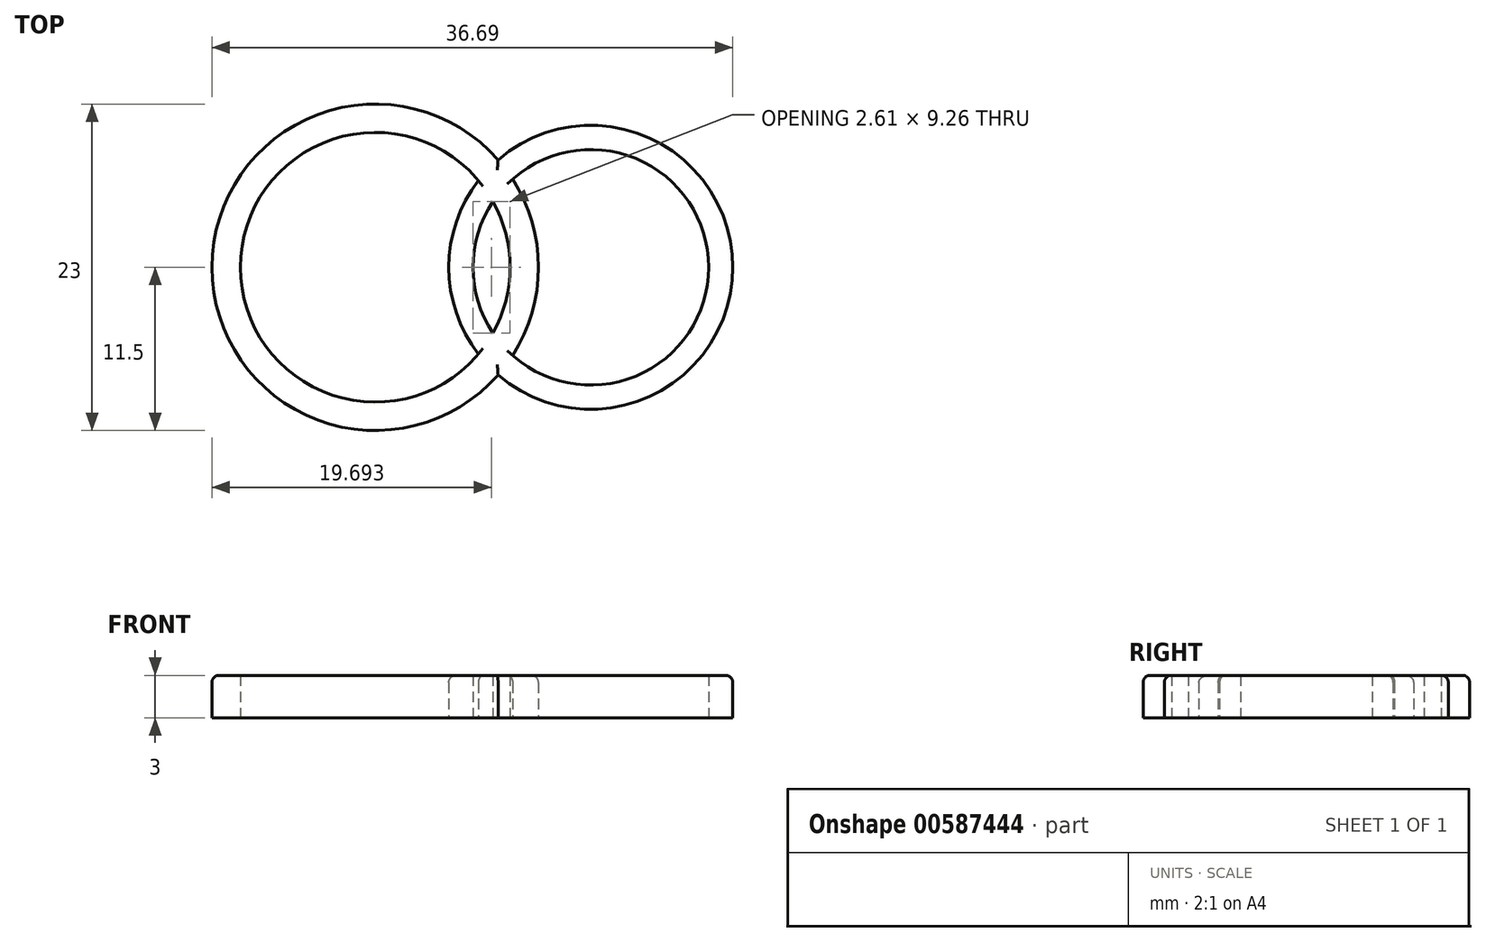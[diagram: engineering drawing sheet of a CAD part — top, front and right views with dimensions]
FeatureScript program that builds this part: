
annotation { "Feature Type Name" : "Feature", "Feature Type Description" : "" }
export const myFeature = defineFeature(function(context is Context, id is Id, definition is map)
    precondition{}
    {
        {
            var Q0;
            Q0=qCreatedBy(makeId("Top.planeOp"),FACE);
            var sketch = newSketch(context, id + "F0", { "sketchPlane" : qUnion([Q0])});
            skCircle(sketch, "E0", {"center": v(0, 0) * mm, "radius": 11.5 * mm});
            skCircle(sketch, "E1", {"center": v(0, 0) * mm, "radius": 9.5 * mm});
            skCircle(sketch, "E2", {"center": v(15.19, 0) * mm, "radius": 10 * mm});
            skCircle(sketch, "E3", {"center": v(15.19, 0) * mm, "radius": 8.3 * mm});
            skSolve(sketch);
        }
        {
            var Q0;
            {var subQ0=sQuery(id+"F0.wireOp",EDGE,"E2");var subQ1=sQuery(id+"F0.wireOp",EDGE,"E0");var subQ2=makeQuery(id+"F0.imprint","INTERSECT",VERTEX,{"disambiguationData":[OD(0.0)],"derivedFrom":[subQ1,subQ0]});Q0=makeQuery(id+"F0.imprint","IMPRINT",FACE,{"disambiguationData":[TD([[makeQuery(id+"F0.imprint","IMPRINT",EDGE,{"disambiguationData":[TD([[subQ2,-1.0]])],"derivedFrom":subQ1}),1.0]])]});}
            var Q1;
            {var subQ0=sQuery(id+"F0.wireOp",EDGE,"E2");var subQ1=sQuery(id+"F0.wireOp",EDGE,"E0");var subQ2=makeQuery(id+"F0.imprint","INTERSECT",VERTEX,{"disambiguationData":[OD(0.0)],"derivedFrom":[subQ1,subQ0]});Q1=makeQuery(id+"F0.imprint","IMPRINT",FACE,{"disambiguationData":[TD([[makeQuery(id+"F0.imprint","IMPRINT",EDGE,{"disambiguationData":[TD([[subQ2,1.0]])],"derivedFrom":subQ1}),1.0]])]});}
            var Q2;
            {var subQ0=sQuery(id+"F0.wireOp",EDGE,"E3");var subQ1=sQuery(id+"F0.wireOp",EDGE,"E0");var subQ2=makeQuery(id+"F0.imprint","INTERSECT",VERTEX,{"disambiguationData":[OD(0.0)],"derivedFrom":[subQ1,subQ0]});Q2=makeQuery(id+"F0.imprint","IMPRINT",FACE,{"disambiguationData":[TD([[makeQuery(id+"F0.imprint","IMPRINT",EDGE,{"disambiguationData":[TD([[subQ2,1.0]])],"derivedFrom":subQ1}),1.0]])]});}
            var Q3;
            {var subQ0=sQuery(id+"F0.wireOp",EDGE,"E2");var subQ1=sQuery(id+"F0.wireOp",EDGE,"E0");var subQ2=makeQuery(id+"F0.imprint","INTERSECT",VERTEX,{"disambiguationData":[OD(1.0)],"derivedFrom":[subQ1,subQ0]});Q3=makeQuery(id+"F0.imprint","IMPRINT",FACE,{"disambiguationData":[TD([[makeQuery(id+"F0.imprint","IMPRINT",EDGE,{"disambiguationData":[TD([[subQ2,-1.0]])],"derivedFrom":subQ1}),1.0]])]});}
            var Q4;
            {var subQ0=sQuery(id+"F0.wireOp",EDGE,"E2");var subQ1=sQuery(id+"F0.wireOp",EDGE,"E1");var subQ2=makeQuery(id+"F0.imprint","INTERSECT",VERTEX,{"disambiguationData":[OD(0.0)],"derivedFrom":[subQ1,subQ0]});Q4=makeQuery(id+"F0.imprint","IMPRINT",FACE,{"disambiguationData":[TD([[makeQuery(id+"F0.imprint","IMPRINT",EDGE,{"disambiguationData":[TD([[subQ2,1.0]])],"derivedFrom":subQ1}),1.0]])]});}
            var Q5;
            {var subQ0=sQuery(id+"F0.wireOp",EDGE,"E2");var subQ1=sQuery(id+"F0.wireOp",EDGE,"E0");var subQ2=makeQuery(id+"F0.imprint","INTERSECT",VERTEX,{"disambiguationData":[OD(0.0)],"derivedFrom":[subQ1,subQ0]});Q5=makeQuery(id+"F0.imprint","IMPRINT",FACE,{"disambiguationData":[TD([[makeQuery(id+"F0.imprint","IMPRINT",EDGE,{"disambiguationData":[TD([[subQ2,1.0]])],"derivedFrom":subQ1}),-1.0]])]});}
            extrude(context, id + "F1", {"entities" : qUnion([Q0, Q1, Q2, Q3, Q4, Q5]), "depth" : 3 * mm, "offsetDistance" : 25 * mm});
        }
        {
            var Q0;
            {var subQ0=sQuery(id+"F0.wireOp",EDGE,"E2");var subQ1=sQuery(id+"F0.wireOp",EDGE,"E0");Q0=makeQuery(id+"F1.opExtrude","CAP_EDGE",EDGE,{"disambiguationData":[OSD([subQ1]),TDD([makeQuery(id+"F0.imprint","IMPRINT",EDGE,{"disambiguationData":[TD([[makeQuery(id+"F0.imprint","INTERSECT",VERTEX,{"disambiguationData":[OD(0.0)],"derivedFrom":[subQ1,subQ0]}),-1.0]])],"derivedFrom":subQ1})])],"isStart":false});}
            var Q1;
            {var subQ0=sQuery(id+"F0.wireOp",EDGE,"E2");var subQ1=sQuery(id+"F0.wireOp",EDGE,"E0");Q1=makeQuery(id+"F1.opExtrude","CAP_EDGE",EDGE,{"disambiguationData":[OSD([subQ0]),TDD([makeQuery(id+"F0.imprint","IMPRINT",EDGE,{"disambiguationData":[TD([[makeQuery(id+"F0.imprint","INTERSECT",VERTEX,{"disambiguationData":[OD(0.0)],"derivedFrom":[subQ1,subQ0]}),1.0]])],"derivedFrom":subQ0})])],"isStart":false});}
            var Q2;
            {var subQ0=sQuery(id+"F0.wireOp",EDGE,"E3");var subQ1=sQuery(id+"F0.wireOp",EDGE,"E0");Q2=makeQuery(id+"F1.opExtrude","CAP_EDGE",EDGE,{"disambiguationData":[OSD([subQ1]),TDD([makeQuery(id+"F0.imprint","IMPRINT",EDGE,{"disambiguationData":[TD([[makeQuery(id+"F0.imprint","INTERSECT",VERTEX,{"disambiguationData":[OD(0.0)],"derivedFrom":[subQ1,subQ0]}),1.0]])],"derivedFrom":subQ1})])],"isStart":false});}
            var Q3;
            {var subQ0=sQuery(id+"F0.wireOp",EDGE,"E2");var subQ1=sQuery(id+"F0.wireOp",EDGE,"E1");Q3=makeQuery(id+"F1.opExtrude","CAP_EDGE",EDGE,{"disambiguationData":[OSD([subQ0]),TDD([makeQuery(id+"F0.imprint","IMPRINT",EDGE,{"disambiguationData":[TD([[makeQuery(id+"F0.imprint","INTERSECT",VERTEX,{"disambiguationData":[OD(0.0)],"derivedFrom":[subQ1,subQ0]}),-1.0]])],"derivedFrom":subQ0})])],"isStart":false});}
            fillet(context, id + "F2", {"entities" : qUnion([Q0, Q1, Q2, Q3]), "radius" : 0.5 * mm, "tangentPropagation" : true, "allowEdgeOverflow" : false});
        }
    });
